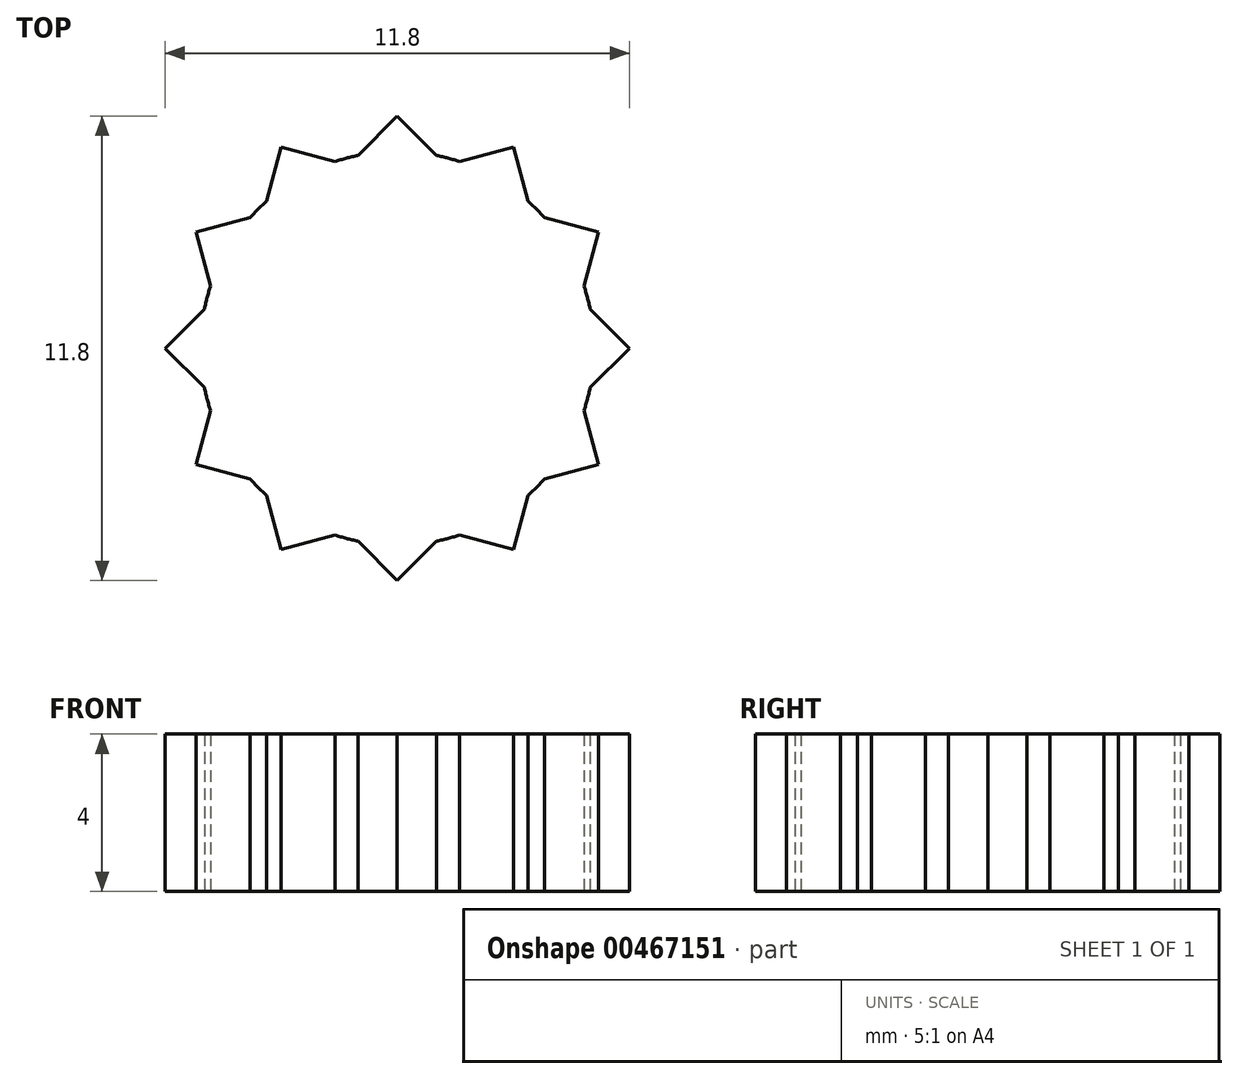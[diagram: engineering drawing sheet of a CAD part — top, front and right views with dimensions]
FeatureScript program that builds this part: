
annotation { "Feature Type Name" : "Feature", "Feature Type Description" : "" }
export const myFeature = defineFeature(function(context is Context, id is Id, definition is map)
    precondition{}
    {
        {
            var Q0;
            Q0=qCreatedBy(makeId("Top.planeOp"),FACE);
            var sketch = newSketch(context, id + "F0", { "sketchPlane" : qUnion([Q0])});
            skCircle(sketch, "E0", {"center": v(0, 0) * mm, "radius": 5 * mm});
            skLineSegment(sketch, "E1", {"start": v(-1, 4.9) * mm, "end": v(1, 4.9) * mm});
            skLineSegment(sketch, "E2", {"start": v(-1, 4.9) * mm, "end": v(0, 5.9) * mm});
            skLineSegment(sketch, "E3", {"start": v(0, 5.9) * mm, "end": v(1, 4.9) * mm});
            skLineSegment(sketch, "E4.1.0", {"start": v(-3.32, 3.74) * mm, "end": v(-2.95, 5.1) * mm});
            skLineSegment(sketch, "E4.1.1", {"start": v(-2.95, 5.1) * mm, "end": v(-1.58, 4.74) * mm});
            skLineSegment(sketch, "E4.2.0", {"start": v(-4.74, 1.58) * mm, "end": v(-5.1, 2.95) * mm});
            skLineSegment(sketch, "E4.2.1", {"start": v(-5.1, 2.95) * mm, "end": v(-3.74, 3.32) * mm});
            skLineSegment(sketch, "E4.3.0", {"start": v(-4.9, -1) * mm, "end": v(-5.9, 0) * mm});
            skLineSegment(sketch, "E4.3.1", {"start": v(-5.9, 0) * mm, "end": v(-4.9, 1) * mm});
            skLineSegment(sketch, "E4.4.0", {"start": v(-3.74, -3.32) * mm, "end": v(-5.1, -2.95) * mm});
            skLineSegment(sketch, "E4.4.1", {"start": v(-5.1, -2.95) * mm, "end": v(-4.74, -1.58) * mm});
            skLineSegment(sketch, "E4.5.0", {"start": v(-1.58, -4.74) * mm, "end": v(-2.95, -5.1) * mm});
            skLineSegment(sketch, "E4.5.1", {"start": v(-2.95, -5.1) * mm, "end": v(-3.32, -3.74) * mm});
            skLineSegment(sketch, "E4.6.0", {"start": v(1, -4.9) * mm, "end": v(0, -5.9) * mm});
            skLineSegment(sketch, "E4.6.1", {"start": v(0, -5.9) * mm, "end": v(-1, -4.9) * mm});
            skLineSegment(sketch, "E4.7.0", {"start": v(3.32, -3.74) * mm, "end": v(2.95, -5.1) * mm});
            skLineSegment(sketch, "E4.7.1", {"start": v(2.95, -5.1) * mm, "end": v(1.58, -4.74) * mm});
            skLineSegment(sketch, "E4.8.0", {"start": v(4.74, -1.58) * mm, "end": v(5.1, -2.95) * mm});
            skLineSegment(sketch, "E4.8.1", {"start": v(5.1, -2.95) * mm, "end": v(3.74, -3.32) * mm});
            skLineSegment(sketch, "E4.9.0", {"start": v(4.9, 1) * mm, "end": v(5.9, 0) * mm});
            skLineSegment(sketch, "E4.9.1", {"start": v(5.9, 0) * mm, "end": v(4.9, -1) * mm});
            skLineSegment(sketch, "E4.10.0", {"start": v(3.74, 3.32) * mm, "end": v(5.1, 2.95) * mm});
            skLineSegment(sketch, "E4.10.1", {"start": v(5.1, 2.95) * mm, "end": v(4.74, 1.58) * mm});
            skLineSegment(sketch, "E4.11.0", {"start": v(1.58, 4.74) * mm, "end": v(2.95, 5.1) * mm});
            skLineSegment(sketch, "E4.11.1", {"start": v(2.95, 5.1) * mm, "end": v(3.32, 3.74) * mm});
            skSolve(sketch);
        }
        {
            var Q0;
            {var subQ0=sQuery(id+"F0.wireOp",EDGE,"E1");Q0=makeQuery(id+"F0.imprint","IMPRINT",FACE,{"disambiguationData":[TD([[makeQuery(id+"F0.imprint","IMPRINT",EDGE,{"derivedFrom":subQ0}),-1.0]])]});}
            var Q1;
            {var subQ0=sQuery(id+"F0.wireOp",EDGE,"E1");Q1=makeQuery(id+"F0.imprint","IMPRINT",FACE,{"disambiguationData":[TD([[makeQuery(id+"F0.imprint","IMPRINT",EDGE,{"derivedFrom":subQ0}),1.0]])]});}
            var Q2;
            {var subQ0=sQuery(id+"F0.wireOp",EDGE,"E4.1.0");Q2=makeQuery(id+"F0.imprint","IMPRINT",FACE,{"disambiguationData":[TD([[makeQuery(id+"F0.imprint","IMPRINT",EDGE,{"derivedFrom":subQ0}),-1.0]])]});}
            var Q3;
            {var subQ0=sQuery(id+"F0.wireOp",EDGE,"E2");Q3=makeQuery(id+"F0.imprint","IMPRINT",FACE,{"disambiguationData":[TD([[makeQuery(id+"F0.imprint","IMPRINT",EDGE,{"derivedFrom":subQ0}),-1.0]])]});}
            var Q4;
            {var subQ0=sQuery(id+"F0.wireOp",EDGE,"E4.11.0");Q4=makeQuery(id+"F0.imprint","IMPRINT",FACE,{"disambiguationData":[TD([[makeQuery(id+"F0.imprint","IMPRINT",EDGE,{"derivedFrom":subQ0}),-1.0]])]});}
            var Q5;
            {var subQ0=sQuery(id+"F0.wireOp",EDGE,"E4.10.0");Q5=makeQuery(id+"F0.imprint","IMPRINT",FACE,{"disambiguationData":[TD([[makeQuery(id+"F0.imprint","IMPRINT",EDGE,{"derivedFrom":subQ0}),-1.0]])]});}
            var Q6;
            {var subQ0=sQuery(id+"F0.wireOp",EDGE,"E4.9.0");Q6=makeQuery(id+"F0.imprint","IMPRINT",FACE,{"disambiguationData":[TD([[makeQuery(id+"F0.imprint","IMPRINT",EDGE,{"derivedFrom":subQ0}),-1.0]])]});}
            var Q7;
            {var subQ0=sQuery(id+"F0.wireOp",EDGE,"E4.8.0");Q7=makeQuery(id+"F0.imprint","IMPRINT",FACE,{"disambiguationData":[TD([[makeQuery(id+"F0.imprint","IMPRINT",EDGE,{"derivedFrom":subQ0}),-1.0]])]});}
            var Q8;
            {var subQ0=sQuery(id+"F0.wireOp",EDGE,"E4.7.0");Q8=makeQuery(id+"F0.imprint","IMPRINT",FACE,{"disambiguationData":[TD([[makeQuery(id+"F0.imprint","IMPRINT",EDGE,{"derivedFrom":subQ0}),-1.0]])]});}
            var Q9;
            {var subQ0=sQuery(id+"F0.wireOp",EDGE,"E4.6.0");Q9=makeQuery(id+"F0.imprint","IMPRINT",FACE,{"disambiguationData":[TD([[makeQuery(id+"F0.imprint","IMPRINT",EDGE,{"derivedFrom":subQ0}),-1.0]])]});}
            var Q10;
            {var subQ0=sQuery(id+"F0.wireOp",EDGE,"E4.5.0");Q10=makeQuery(id+"F0.imprint","IMPRINT",FACE,{"disambiguationData":[TD([[makeQuery(id+"F0.imprint","IMPRINT",EDGE,{"derivedFrom":subQ0}),-1.0]])]});}
            var Q11;
            {var subQ0=sQuery(id+"F0.wireOp",EDGE,"E4.4.0");Q11=makeQuery(id+"F0.imprint","IMPRINT",FACE,{"disambiguationData":[TD([[makeQuery(id+"F0.imprint","IMPRINT",EDGE,{"derivedFrom":subQ0}),-1.0]])]});}
            var Q12;
            {var subQ0=sQuery(id+"F0.wireOp",EDGE,"E4.3.0");Q12=makeQuery(id+"F0.imprint","IMPRINT",FACE,{"disambiguationData":[TD([[makeQuery(id+"F0.imprint","IMPRINT",EDGE,{"derivedFrom":subQ0}),-1.0]])]});}
            var Q13;
            {var subQ0=sQuery(id+"F0.wireOp",EDGE,"E4.2.0");Q13=makeQuery(id+"F0.imprint","IMPRINT",FACE,{"disambiguationData":[TD([[makeQuery(id+"F0.imprint","IMPRINT",EDGE,{"derivedFrom":subQ0}),-1.0]])]});}
            extrude(context, id + "F1", {"entities" : qUnion([Q0, Q1, Q2, Q3, Q4, Q5, Q6, Q7, Q8, Q9, Q10, Q11, Q12, Q13]), "depth" : 4 * mm});
        }
    });
